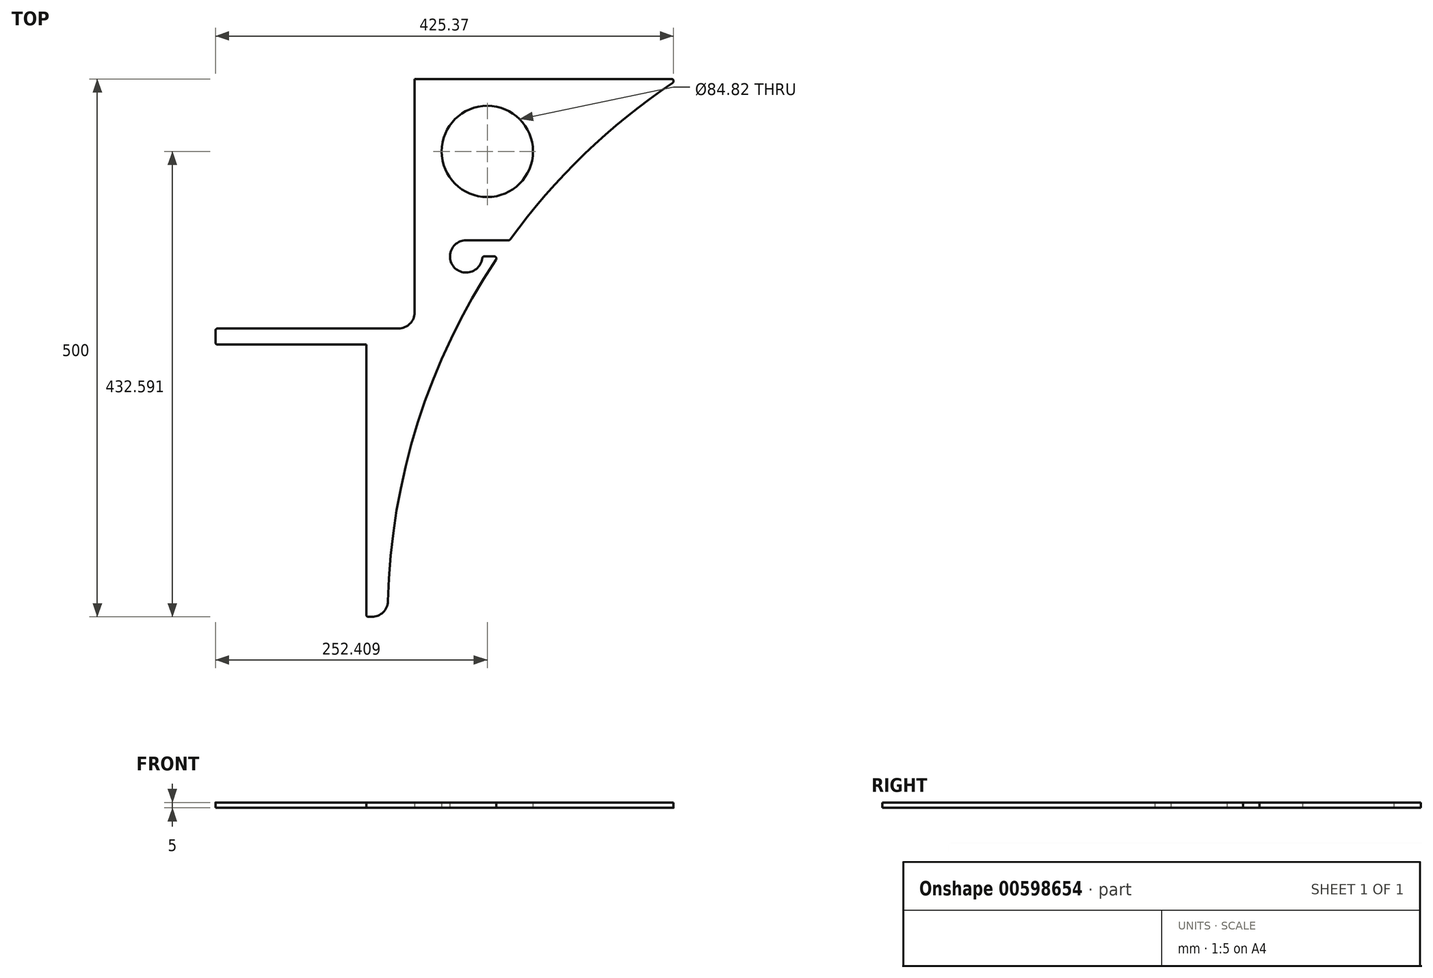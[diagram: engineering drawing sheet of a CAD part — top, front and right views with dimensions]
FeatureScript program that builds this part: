
annotation { "Feature Type Name" : "Feature", "Feature Type Description" : "" }
export const myFeature = defineFeature(function(context is Context, id is Id, definition is map)
    precondition{}
    {
        {
            var Q0;
            Q0=qCreatedBy(makeId("Top.planeOp"),FACE);
            var sketch = newSketch(context, id + "F0", { "sketchPlane" : qUnion([Q0])});
            skLineSegment(sketch, "E0", {"start": v(145, 253) * mm, "end": v(5, 253) * mm});
            skLineSegment(sketch, "E1", {"start": v(190, 268) * mm, "end": v(190, 500) * mm});
            skLineSegment(sketch, "E2", {"start": v(190, 500) * mm, "end": v(435, 500) * mm});
            skLineSegment(sketch, "E3", {"start": v(145, 253) * mm, "end": v(145, 0) * mm});
            skLineSegment(sketch, "E4", {"start": v(0, 0) * mm, "end": v(0, 500) * mm, "construction": true});
            skLineSegment(sketch, "E5", {"start": v(495, 520) * mm, "end": v(495, 480) * mm, "construction": true});
            skLineSegment(sketch, "E6", {"start": v(375, 520) * mm, "end": v(375, 480) * mm, "construction": true});
            skLineSegment(sketch, "E7", {"start": v(145, 0) * mm, "end": v(165, 0) * mm});
            skArc(sketch, "E8", {"start": v(435, 500) * mm, "mid": v(349.7, 432.18) * mm, "end": v(278.13, 350) * mm});
            skLineSegment(sketch, "E9", {"start": v(5, 253) * mm, "end": v(5, 268) * mm});
            skLineSegment(sketch, "E10", {"start": v(5, 268) * mm, "end": v(190, 268) * mm});
            skCircle(sketch, "E11", {"center": v(257.4, 432.6) * mm, "radius": 42.4 * mm});
            skLineSegment(sketch, "E12", {"start": v(278.13, 350) * mm, "end": v(237.74, 350) * mm});
            skArc(sketch, "E13", {"start": v(237.74, 350) * mm, "mid": v(227.13, 324.4) * mm, "end": v(252.74, 335) * mm});
            skLineSegment(sketch, "E14", {"start": v(252.74, 335) * mm, "end": v(267.65, 335) * mm});
            skArc(sketch, "E15.trimOffspring", {"start": v(267.65, 335) * mm, "mid": v(191.24, 175.19) * mm, "end": v(165, 0) * mm});
            skSolve(sketch);
        }
        {
            var Q0;
            Q0=makeQuery(id+"F0.imprint","IMPRINT",FACE,{"disambiguationData":[TD([[makeQuery(id+"F0.imprint","IMPRINT",EDGE,{"derivedFrom":sQuery(id+"F0.wireOp",EDGE,"E0")}),-1.0]])]});
            extrude(context, id + "F1", {"entities" : qUnion([Q0]), "endBound" : BoundingType.SYMMETRIC, "depth" : 5 * mm, "offsetDistance" : 25 * mm});
        }
        {
            var Q0;
            Q0=makeQuery(id+"F1.opExtrude","SWEPT_EDGE",EDGE,{"disambiguationData":[OSD([sQuery(id+"F0.wireOp",EDGE,"E2"),sQuery(id+"F0.wireOp",EDGE,"E8")])]});
            var Q1;
            Q1=makeQuery(id+"F1.opExtrude","SWEPT_EDGE",EDGE,{"disambiguationData":[OSD([sQuery(id+"F0.wireOp",EDGE,"E3"),sQuery(id+"F0.wireOp",EDGE,"E7")])]});
            var Q2;
            Q2=makeQuery(id+"F1.opExtrude","SWEPT_EDGE",EDGE,{"disambiguationData":[OSD([sQuery(id+"F0.wireOp",EDGE,"E9"),sQuery(id+"F0.wireOp",EDGE,"E10")])]});
            var Q3;
            Q3=makeQuery(id+"F1.opExtrude","SWEPT_EDGE",EDGE,{"disambiguationData":[OSD([sQuery(id+"F0.wireOp",EDGE,"E0"),sQuery(id+"F0.wireOp",EDGE,"E9")])]});
            var Q4;
            Q4=makeQuery(id+"F1.opExtrude","SWEPT_EDGE",EDGE,{"disambiguationData":[OSD([sQuery(id+"F0.wireOp",EDGE,"E8"),sQuery(id+"F0.wireOp",EDGE,"E12")])]});
            var Q5;
            Q5=makeQuery(id+"F1.opExtrude","SWEPT_EDGE",EDGE,{"disambiguationData":[OSD([sQuery(id+"F0.wireOp",EDGE,"E14"),sQuery(id+"F0.wireOp",EDGE,"E15.trimOffspring")])]});
            var Q6;
            Q6=makeQuery(id+"F1.opExtrude","SWEPT_EDGE",EDGE,{"disambiguationData":[OSD([sQuery(id+"F0.wireOp",EDGE,"E13"),sQuery(id+"F0.wireOp",EDGE,"E14")])]});
            fillet(context, id + "F2", {"entities" : qUnion([Q0, Q1, Q2, Q3, Q4, Q5, Q6]), "radius" : 2 * mm, "tangentPropagation" : true, "allowEdgeOverflow" : false});
        }
        {
            var Q0;
            Q0=makeQuery(id+"F1.opExtrude","SWEPT_EDGE",EDGE,{"disambiguationData":[OSD([sQuery(id+"F0.wireOp",EDGE,"E1"),sQuery(id+"F0.wireOp",EDGE,"E10")])]});
            var Q1;
            Q1=makeQuery(id+"F1.opExtrude","SWEPT_EDGE",EDGE,{"disambiguationData":[OSD([sQuery(id+"F0.wireOp",EDGE,"E7"),sQuery(id+"F0.wireOp",EDGE,"E15.trimOffspring")])]});
            fillet(context, id + "F3", {"entities" : qUnion([Q0, Q1]), "radius" : 15 * mm, "tangentPropagation" : true, "allowEdgeOverflow" : false});
        }
    });
